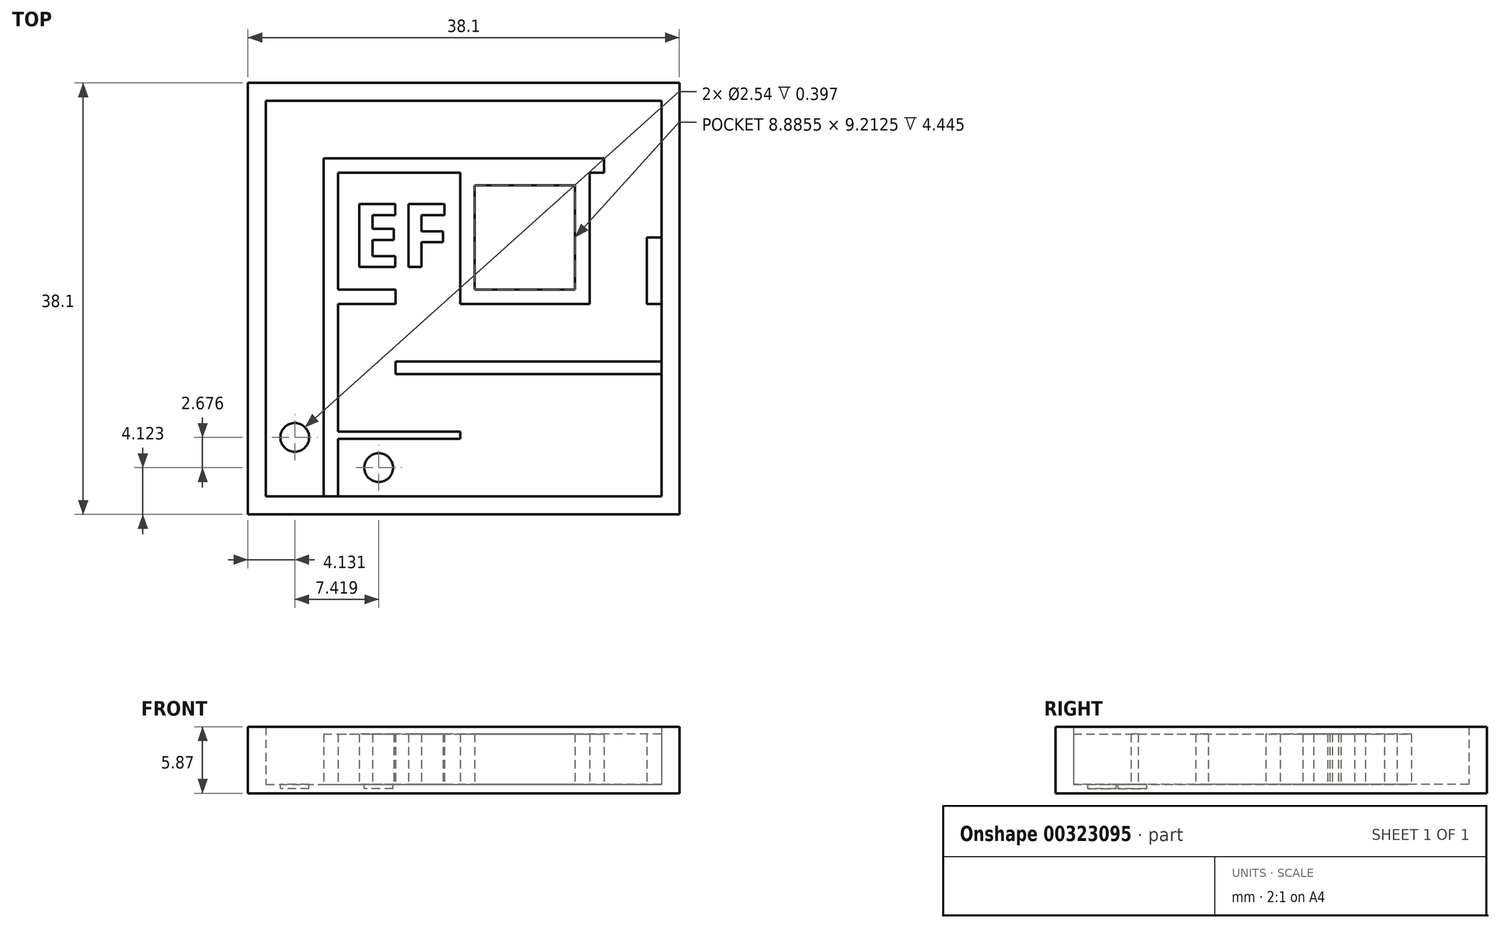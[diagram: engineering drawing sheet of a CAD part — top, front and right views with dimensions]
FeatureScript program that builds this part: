
annotation { "Feature Type Name" : "Feature", "Feature Type Description" : "" }
export const myFeature = defineFeature(function(context is Context, id is Id, definition is map)
    precondition{}
    {
        {
            var Q0;
            Q0=qCreatedBy(makeId("Top.planeOp"),FACE);
            var sketch = newSketch(context, id + "F0", { "sketchPlane" : qUnion([Q0])});
            skLineSegment(sketch, "E0.bottom", {"start": v(-15.74, 15.73) * mm, "end": v(22.36, 15.73) * mm});
            skLineSegment(sketch, "E0.top", {"start": v(-15.74, -22.37) * mm, "end": v(22.36, -22.37) * mm});
            skLineSegment(sketch, "E0.left", {"start": v(-15.74, 15.73) * mm, "end": v(-15.74, -22.37) * mm});
            skLineSegment(sketch, "E0.right", {"start": v(22.36, 15.73) * mm, "end": v(22.36, -22.37) * mm});
            skSolve(sketch);
        }
        {
            var Q0;
            Q0=makeQuery(id+"F0.imprint","IMPRINT",FACE,{"disambiguationData":[TD([[makeQuery(id+"F0.imprint","IMPRINT",EDGE,{"derivedFrom":sQuery(id+"F0.wireOp",EDGE,"E0.bottom")}),-1.0]])]});
            extrude(context, id + "F1", {"entities" : qUnion([Q0]), "depth" : 0.8 * mm});
        }
        {
            var Q0;
            Q0=makeQuery(id+"F1.opExtrude","CAP_FACE",FACE,{"disambiguationData":[OSD([sQuery(id+"F0.wireOp",EDGE,"E0.bottom"),sQuery(id+"F0.wireOp",EDGE,"E0.top"),sQuery(id+"F0.wireOp",EDGE,"E0.left"),sQuery(id+"F0.wireOp",EDGE,"E0.right")])],"isStart":false});
            var sketch = newSketch(context, id + "F2", { "sketchPlane" : qUnion([Q0])});
            skLineSegment(sketch, "E1.0", {"start": v(-14.15, 14.14) * mm, "end": v(20.78, 14.14) * mm});
            skLineSegment(sketch, "E1.1", {"start": v(-14.15, 14.14) * mm, "end": v(-14.15, -20.79) * mm});
            skLineSegment(sketch, "E1.2", {"start": v(-14.15, -20.79) * mm, "end": v(20.78, -20.79) * mm});
            skLineSegment(sketch, "E1.3", {"start": v(20.78, 14.14) * mm, "end": v(20.78, -20.79) * mm});
            skSolve(sketch);
        }
        {
            var Q0;
            Q0=makeQuery(id+"F2.imprint","IMPRINT",FACE,{"disambiguationData":[TD([[makeQuery(id+"F2.imprint","IMPRINT",EDGE,{"derivedFrom":sQuery(id+"F2.wireOp",EDGE,"E1.0")}),1.0]])]});
            extrude(context, id + "F3", {"entities" : qUnion([Q0]), "operationType" : NewBodyOperationType.ADD, "depth" : 5.08 * mm});
        }
        {
            var Q0;
            Q0=makeQuery(id+"F1.opExtrude","CAP_FACE",FACE,{"disambiguationData":[OSD([sQuery(id+"F0.wireOp",EDGE,"E0.bottom"),sQuery(id+"F0.wireOp",EDGE,"E0.top"),sQuery(id+"F0.wireOp",EDGE,"E0.left"),sQuery(id+"F0.wireOp",EDGE,"E0.right")])],"isStart":false});
            var sketch = newSketch(context, id + "F4", { "sketchPlane" : qUnion([Q0])});
            skLineSegment(sketch, "E2.bottom", {"start": v(-9.07, -20.79) * mm, "end": v(-7.8, -20.79) * mm});
            skLineSegment(sketch, "E2.top", {"start": v(-9.07, 9.06) * mm, "end": v(-7.8, 9.06) * mm});
            skLineSegment(sketch, "E2.left", {"start": v(-9.07, -20.79) * mm, "end": v(-9.07, 9.06) * mm});
            skLineSegment(sketch, "E2.right", {"start": v(-7.8, -20.79) * mm, "end": v(-7.8, 7.79) * mm});
            skLineSegment(sketch, "E3.bottom", {"start": v(-7.8, 9.06) * mm, "end": v(15.7, 9.06) * mm});
            skLineSegment(sketch, "E3.top", {"start": v(-7.8, 7.79) * mm, "end": v(3, 7.79) * mm});
            skLineSegment(sketch, "E3.right", {"start": v(15.7, 9.06) * mm, "end": v(15.7, 7.79) * mm});
            skLineSegment(sketch, "E4.top", {"start": v(3, -3.8) * mm, "end": v(14.43, -3.8) * mm});
            skLineSegment(sketch, "E4.left", {"start": v(3, 7.79) * mm, "end": v(3, -3.8) * mm});
            skLineSegment(sketch, "E4.right", {"start": v(14.43, 7.79) * mm, "end": v(14.43, -3.8) * mm});
            skLineSegment(sketch, "E5.bottom", {"start": v(20.78, 2.1) * mm, "end": v(19.5, 2.1) * mm});
            skLineSegment(sketch, "E5.top", {"start": v(20.78, -3.8) * mm, "end": v(19.5, -3.8) * mm});
            skLineSegment(sketch, "E5.left", {"start": v(20.78, 2.1) * mm, "end": v(20.78, -3.8) * mm});
            skLineSegment(sketch, "E5.right", {"start": v(19.5, 2.1) * mm, "end": v(19.5, -3.8) * mm});
            skLineSegment(sketch, "E6.bottom", {"start": v(-7.8, -3.8) * mm, "end": v(-2.72, -3.8) * mm});
            skLineSegment(sketch, "E6.top", {"start": v(-7.8, -2.53) * mm, "end": v(-2.72, -2.53) * mm});
            skLineSegment(sketch, "E6.left", {"start": v(-7.8, -2.53) * mm, "end": v(-7.8, -3.8) * mm});
            skLineSegment(sketch, "E6.right", {"start": v(-2.72, -2.53) * mm, "end": v(-2.72, -3.8) * mm});
            skLineSegment(sketch, "E7.bottom", {"start": v(20.78, -10) * mm, "end": v(-2.72, -10) * mm});
            skLineSegment(sketch, "E7.top", {"start": v(20.78, -8.88) * mm, "end": v(-2.72, -8.88) * mm});
            skLineSegment(sketch, "E7.left", {"start": v(20.78, -10) * mm, "end": v(20.78, -8.88) * mm});
            skLineSegment(sketch, "E7.right", {"start": v(-2.72, -10) * mm, "end": v(-2.72, -8.88) * mm});
            skLineSegment(sketch, "E8.bottom", {"start": v(-7.8, -15.07) * mm, "end": v(3.02, -15.07) * mm});
            skLineSegment(sketch, "E8.top", {"start": v(-7.8, -15.7) * mm, "end": v(3.02, -15.7) * mm});
            skLineSegment(sketch, "E8.left", {"start": v(-7.8, -15.07) * mm, "end": v(-7.8, -15.7) * mm});
            skLineSegment(sketch, "E8.right", {"start": v(3.02, -15.07) * mm, "end": v(3.02, -15.7) * mm});
            skLineSegment(sketch, "E9.trimOffspring", {"start": v(14.43, 7.79) * mm, "end": v(15.7, 7.79) * mm});
            skLineSegment(sketch, "E10.0", {"start": v(13.16, 6.68) * mm, "end": v(13.16, -2.53) * mm});
            skLineSegment(sketch, "E10.1", {"start": v(4.27, -2.53) * mm, "end": v(13.16, -2.53) * mm});
            skLineSegment(sketch, "E10.2", {"start": v(4.27, 6.68) * mm, "end": v(4.27, -2.53) * mm});
            skLineSegment(sketch, "E11", {"start": v(13.16, 6.68) * mm, "end": v(4.27, 6.68) * mm});
            skLineSegment(sketch, "E12", {"start": v(-14.15, -20.79) * mm, "end": v(-9.07, -20.79) * mm});
            skCircle(sketch, "E13", {"center": v(-11.6, -15.57) * mm, "radius": 1.27 * mm});
            skPoint(sketch, "E13.centerSnap0", {"position": v(-11.6, -20.79) * mm});
            skLineSegment(sketch, "E14", {"start": v(-7.8, -20.79) * mm, "end": v(-7.8, -15.7) * mm});
            skCircle(sketch, "E15", {"center": v(-4.19, -18.25) * mm, "radius": 1.27 * mm});
            skPoint(sketch, "E15.centerSnap0", {"position": v(-7.8, -18.25) * mm});
            skLineSegment(sketch, "E16", {"start": v(-7.8, 7.79) * mm, "end": v(-7.8, -2.53) * mm});
            skText(sketch, "E17", { "text": "EF", "fontName": "OpenSans-Bold.ttf"});
            const initialGuessF4  = {"E17": [-0.00662, -0.00053, 1, 0, 0.0056]};
            skSetInitialGuess(sketch, initialGuessF4);
            skSolve(sketch);
        }
        {
            var Q0;
            Q0=makeQuery(id+"F4.imprint","IMPRINT",FACE,{"disambiguationData":[TD([[makeQuery(id+"F4.imprint","IMPRINT",EDGE,{"derivedFrom":sQuery(id+"F4.wireOp",EDGE,"E13")}),1.0]])]});
            var Q1;
            Q1=makeQuery(id+"F4.imprint","IMPRINT",FACE,{"disambiguationData":[TD([[makeQuery(id+"F4.imprint","IMPRINT",EDGE,{"derivedFrom":sQuery(id+"F4.wireOp",EDGE,"E15")}),1.0]])]});
            extrude(context, id + "F5", {"entities" : qUnion([Q0, Q1]), "operationType" : NewBodyOperationType.REMOVE, "oppositeDirection" : true, "depth" : 0.4 * mm});
        }
        {
            var Q0;
            Q0=makeQuery(id+"F4.imprint","IMPRINT",FACE,{"disambiguationData":[TD([[makeQuery(id+"F4.imprint","IMPRINT",EDGE,{"derivedFrom":sQuery(id+"F4.wireOp",EDGE,"E2.bottom")}),1.0]])]});
            var Q1;
            Q1=makeQuery(id+"F4.imprint","IMPRINT",FACE,{"disambiguationData":[TD([[makeQuery(id+"F4.imprint","IMPRINT",EDGE,{"derivedFrom":sQuery(id+"F4.wireOp",EDGE,"E7.bottom")}),-1.0]])]});
            var Q2;
            Q2=makeQuery(id+"F4.imprint","IMPRINT",FACE,{"disambiguationData":[TD([[makeQuery(id+"F4.imprint","IMPRINT",EDGE,{"derivedFrom":sQuery(id+"F4.wireOp",EDGE,"E6.bottom")}),1.0]])]});
            var Q3;
            Q3=makeQuery(id+"F4.imprint","IMPRINT",FACE,{"disambiguationData":[TD([[makeQuery(id+"F4.imprint","IMPRINT",EDGE,{"derivedFrom":sQuery(id+"F4.wireOp",EDGE,"E8.bottom")}),-1.0]])]});
            var Q4;
            Q4=makeQuery(id+"F4.imprint","IMPRINT",FACE,{"disambiguationData":[TD([[makeQuery(id+"F4.imprint","IMPRINT",EDGE,{"derivedFrom":sQuery(id+"F4.wireOp",EDGE,"E5.bottom")}),1.0]])]});
            extrude(context, id + "F6", {"entities" : qUnion([Q0, Q1, Q2, Q3, Q4]), "operationType" : NewBodyOperationType.ADD, "depth" : 4.44 * mm});
        }
        {
            var Q0;
            Q0=makeQuery(id+"F4.imprint","IMPRINT",FACE,{"disambiguationData":[TD([[makeQuery(id+"F4.imprint","IMPRINT",EDGE,{"derivedFrom":sQuery(id+"F4.wireOp",EDGE,"E17.sketch_text.stroke-12")}),-1.0]])]});
            var Q1;
            Q1=makeQuery(id+"F4.imprint","IMPRINT",FACE,{"disambiguationData":[TD([[makeQuery(id+"F4.imprint","IMPRINT",EDGE,{"derivedFrom":sQuery(id+"F4.wireOp",EDGE,"E17.sketch_text.stroke-0")}),-1.0]])]});
            extrude(context, id + "F7", {"entities" : qUnion([Q0, Q1]), "operationType" : NewBodyOperationType.ADD, "depth" : 4.44 * mm});
        }
    });
